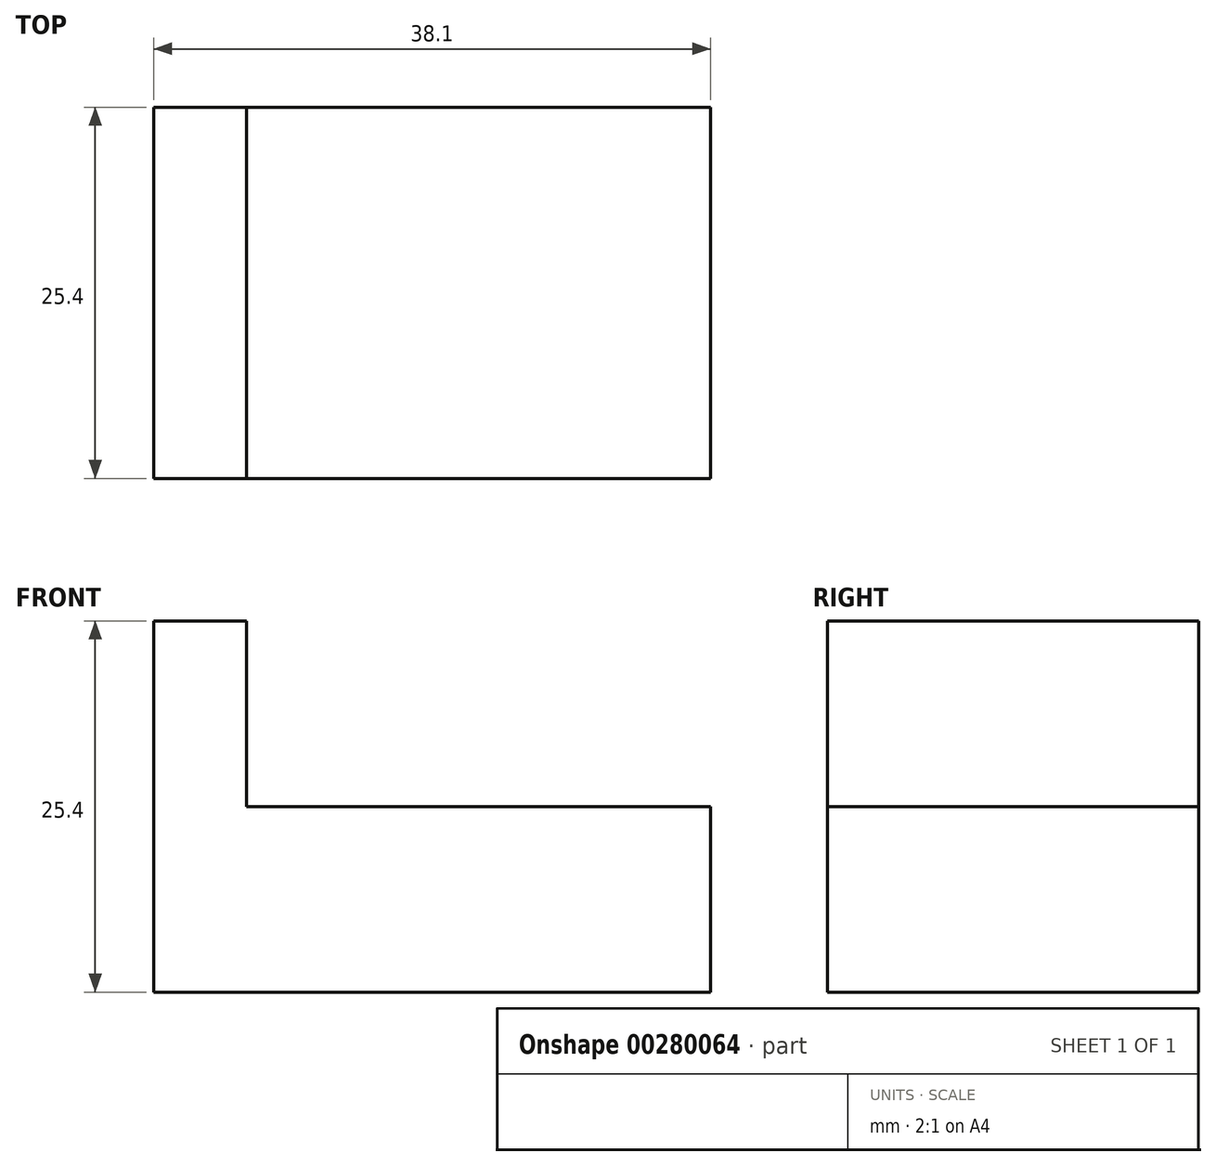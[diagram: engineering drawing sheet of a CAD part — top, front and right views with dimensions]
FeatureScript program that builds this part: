
annotation { "Feature Type Name" : "Feature", "Feature Type Description" : "" }
export const myFeature = defineFeature(function(context is Context, id is Id, definition is map)
    precondition{}
    {
        {
            var Q0;
            Q0=qCreatedBy(makeId("Front.planeOp"),FACE);
            var sketch = newSketch(context, id + "F0", { "sketchPlane" : qUnion([Q0])});
            skLineSegment(sketch, "E0.bottom", {"start": v(0, 0) * mm, "end": v(38.1, 0) * mm});
            skLineSegment(sketch, "E0.top", {"start": v(0, 25.4) * mm, "end": v(38.1, 25.4) * mm});
            skLineSegment(sketch, "E0.left", {"start": v(0, 0) * mm, "end": v(0, 25.4) * mm});
            skLineSegment(sketch, "E0.right", {"start": v(38.1, 0) * mm, "end": v(38.1, 25.4) * mm});
            skSolve(sketch);
        }
        {
            var Q0;
            Q0 = qSketchRegion(id + "F0", true);
            extrude(context, id + "F1", {"entities" : qUnion([Q0]), "depth" : 25.4 * mm});
        }
        {
            var Q0;
            Q0=makeQuery(id+"F1.opExtrude","CAP_FACE",FACE,{"disambiguationData":[OSD([sQuery(id+"F0.wireOp",EDGE,"E0.bottom"),sQuery(id+"F0.wireOp",EDGE,"E0.top"),sQuery(id+"F0.wireOp",EDGE,"E0.left"),sQuery(id+"F0.wireOp",EDGE,"E0.right")])],"isStart":false});
            var sketch = newSketch(context, id + "F2", { "sketchPlane" : qUnion([Q0])});
            skPoint(sketch, "E1", {"position": v(6.35, 25.4) * mm});
            skPoint(sketch, "E2", {"position": v(6.35, 12.7) * mm});
            skLineSegment(sketch, "E3.bottom", {"start": v(6.35, 25.4) * mm, "end": v(38.1, 25.4) * mm});
            skLineSegment(sketch, "E3.top", {"start": v(6.35, 12.7) * mm, "end": v(38.1, 12.7) * mm});
            skLineSegment(sketch, "E3.left", {"start": v(6.35, 25.4) * mm, "end": v(6.35, 12.7) * mm});
            skLineSegment(sketch, "E3.right", {"start": v(38.1, 25.4) * mm, "end": v(38.1, 12.7) * mm});
            skSolve(sketch);
        }
        {
            var Q0;
            Q0=makeQuery(id+"F2.imprint","IMPRINT",FACE,{"disambiguationData":[TD([[makeQuery(id+"F2.imprint","IMPRINT",EDGE,{"derivedFrom":sQuery(id+"F2.wireOp",EDGE,"E3.bottom")}),-1.0]])]});
            extrude(context, id + "F3", {"entities" : qUnion([Q0]), "operationType" : NewBodyOperationType.REMOVE, "endBound" : BoundingType.THROUGH_ALL, "oppositeDirection" : true, "depth" : 25.4 * mm});
        }
    });
